# Revit family: FU_Inspec_Carousel_2-6
name_source: partatom
category: Furniture
units: mm (PartAtom-declared; Revit-internal decimal feet)

## family parameters
Always vertical = Yes
Cut with Voids When Loaded = No
OmniClass Number = 23.40.20.00
OmniClass Title = General Furniture and Specialties
Room Calculation Point = No
Shared = No
Work Plane-Based = No

## types (4) — shared parameters
Assembly Code = E2020
Height = 810 mm
Keynote = 46.B
Manufacturer = Inspec
Two Colored Back = No
URL = https://inspecfurniture.com
Width = 640 mm  [stored 2.09974 ft]
zero-valued in all types: Default Elevation

## per-type parameters (varying)
| type | Back Inside Primary Material | Back Outside Material | Description | Feet Material | Frame Material | Legs Material | Seat Material |
| Carousel 2.4 | Leather - Black | Fabric - Grey Woven | Armchair on a 360° swivel chrome or black powder coat base on a five star base. Upholstered seat and back. | Metal - Black - Matte | Metal - Black - Matte | Metal - Black - Matte | Fabric - Grey Woven |
| Carousel 2.5 | Fabric - Grey Woven | Fabric - Grey Woven | Armchair on a 360° swivel chrome or black powder coat base on a five star base. Upholstered seat and back. With Tilt and height adjustable | Metal - Black - Matte | Metal - Black - Matte | Metal - Black - Matte | Fabric - Grey Woven |
| Carousel 2.6 | Fabric - Orange | Fabric - Orange | Armchair on a 360° swivel chrome or black powder coat base on a five star caster base. Upholstered seat and back. | Metal - Chrome - Polished | Metal - Chrome - Polished | Metal - Chrome - Polished | Fabric - Orange |
| Carousel 2.7 | Leather - Green | Fabric - Grey Woven | Armchair on a 360° swivel chrome or black powder coat base on a five star caster base. Upholstered seat and back. | Metal - Chrome - Polished | Metal - Black - Matte | Metal - Black - Matte | Fabric - Grey Woven |

note: column(s) folded — value = type name in every type: Model

note: [stored X ft] marks values corroborated as IEEE doubles in the binary element streams (Revit-internal decimal feet)

## geometry (parser evidence)
native form markers: Blend x13, Sweep x2
no freeform markers — native parametric forms only
